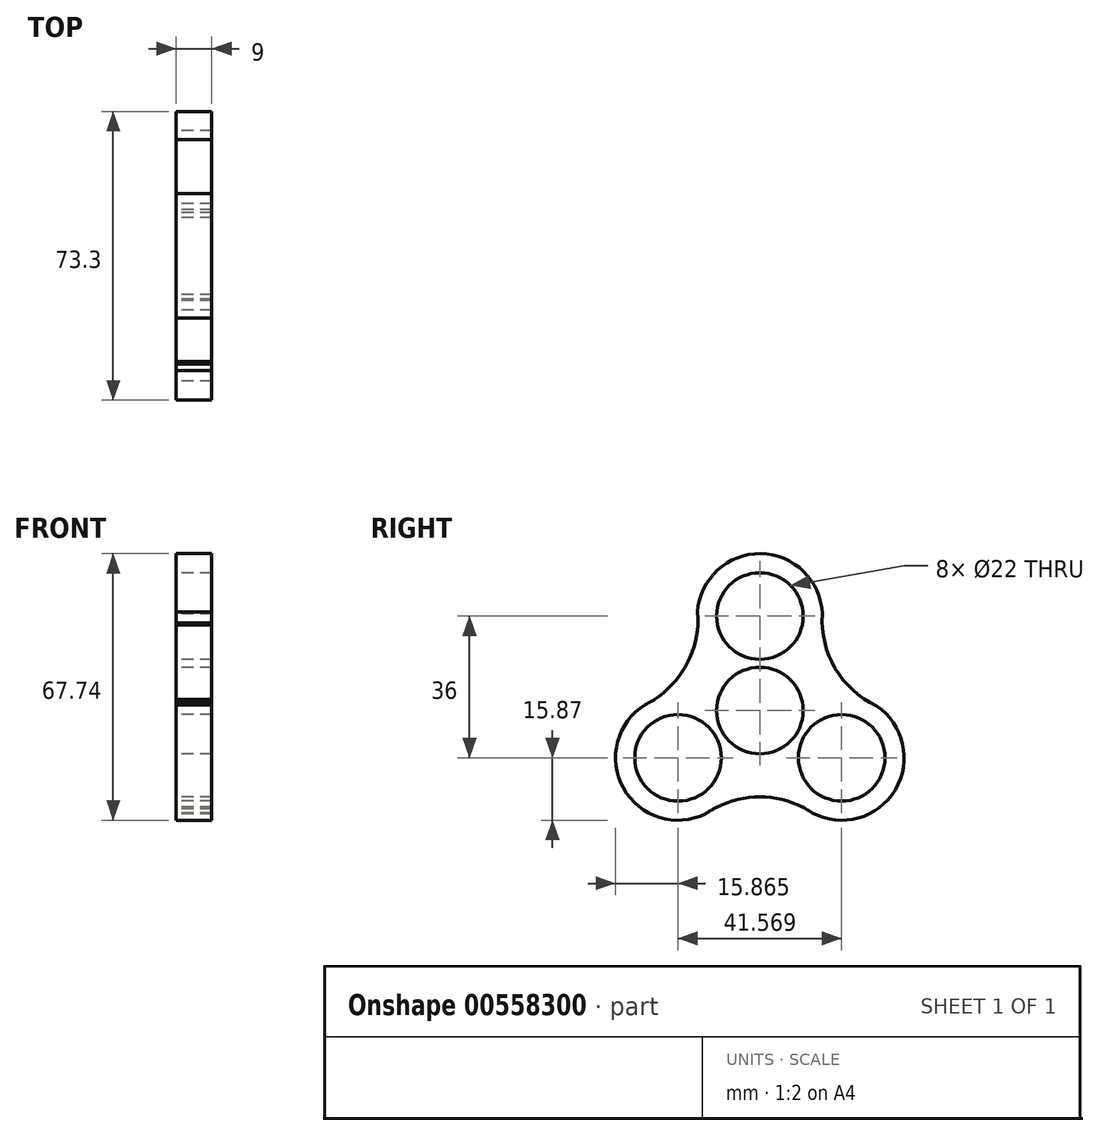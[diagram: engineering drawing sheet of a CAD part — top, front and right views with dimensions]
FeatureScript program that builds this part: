
annotation { "Feature Type Name" : "Feature", "Feature Type Description" : "" }
export const myFeature = defineFeature(function(context is Context, id is Id, definition is map)
    precondition{}
    {
        {
            var Q0;
            Q0=qCreatedBy(makeId("Right.planeOp"),FACE);
            var sketch = newSketch(context, id + "F0", { "sketchPlane" : qUnion([Q0])});
            skLineSegment(sketch, "E0", {"start": v(0, 40) * mm, "end": v(0, 24) * mm});
            skPoint(sketch, "E1", {"position": v(0, 24) * mm});
            skPoint(sketch, "E2.1.0", {"position": v(-20.78, -12) * mm});
            skPoint(sketch, "E2.2.0", {"position": v(20.78, -12) * mm});
            skPoint(sketch, "E2.center", {"position": v(0, 0) * mm});
            skCircle(sketch, "E3", {"center": v(0, 24) * mm, "radius": 11 * mm});
            skCircle(sketch, "E4.1.0", {"center": v(-20.78, -12) * mm, "radius": 11 * mm});
            skCircle(sketch, "E4.2.0", {"center": v(20.78, -12) * mm, "radius": 11 * mm});
            skArc(sketch, "E5.1.0", {"start": v(-26.82, 2.8) * mm, "mid": v(-26.76, 2.76) * mm, "end": v(-26.7, 2.72) * mm});
            skCircle(sketch, "E6", {"center": v(0, 0) * mm, "radius": 11 * mm});
            skPoint(sketch, "E7.start.orphan", {"position": v(10.86, 22.24) * mm});
            skPoint(sketch, "E8.end.orphan", {"position": v(-10.86, 22.24) * mm});
            skArc(sketch, "E9", {"start": v(15.81, 22.66) * mm, "mid": v(-0.46, 39.86) * mm, "end": v(-15.7, 21.76) * mm});
            skArc(sketch, "E10.1.0", {"start": v(-26.7, 2.72) * mm, "mid": v(-34.53, -19.93) * mm, "end": v(-10.99, -24.48) * mm});
            skArc(sketch, "E10.2.0", {"start": v(10.99, -24.48) * mm, "mid": v(34.41, -20.13) * mm, "end": v(27.11, 2.55) * mm});
            skPoint(sketch, "E11.orphan", {"position": v(-11.53, -17.94) * mm});
            skArc(sketch, "E12", {"start": v(15.86, 24.5) * mm, "mid": v(19.14, 10.73) * mm, "end": v(29.6, 1.2) * mm});
            skPoint(sketch, "E12.first.point", {"position": v(15.86, 24.5) * mm});
            skPoint(sketch, "E12.second.point", {"position": v(29.6, 1.2) * mm});
            skPoint(sketch, "E12.third.point", {"position": v(63.5, 27.41) * mm});
            skArc(sketch, "E13.1.0", {"start": v(-29.15, 1.49) * mm, "mid": v(-18.86, 11.21) * mm, "end": v(-15.83, 25.04) * mm});
            skArc(sketch, "E13.2.0", {"start": v(13.29, -25.98) * mm, "mid": v(-0.28, -21.94) * mm, "end": v(-13.77, -26.23) * mm});
            skPoint(sketch, "E14.orphan", {"position": v(-10.08, 9.49) * mm});
            skArc(sketch, "E15.trimOffspring", {"start": v(-15.7, 21.76) * mm, "mid": v(-15.75, 21.78) * mm, "end": v(-15.78, 21.8) * mm});
            skArc(sketch, "E16.trimOffspring", {"start": v(10.98, -24.63) * mm, "mid": v(10.99, -24.55) * mm, "end": v(10.99, -24.48) * mm});
            skArc(sketch, "E17.trimOffspring", {"start": v(-10.99, -24.48) * mm, "mid": v(-10.99, -24.53) * mm, "end": v(-10.99, -24.57) * mm});
            skSolve(sketch);
        }
        {
            var Q0;
            Q0=makeQuery(id+"F0.imprint","IMPRINT",FACE,{"disambiguationData":[TD([[makeQuery(id+"F0.imprint","IMPRINT",EDGE,{"derivedFrom":sQuery(id+"F0.wireOp",EDGE,"E3")}),-1.0]])]});
            var Q1;
            Q1=sQuery(id+"F0.wireOp",EDGE,"E13.1.0");
            var Q2;
            Q2=sQuery(id+"F0.wireOp",EDGE,"E9");
            var Q3;
            Q3=sQuery(id+"F0.wireOp",EDGE,"E12");
            var Q4;
            Q4=sQuery(id+"F0.wireOp",EDGE,"E10.2.0");
            var Q5;
            Q5=sQuery(id+"F0.wireOp",EDGE,"E13.2.0");
            var Q6;
            Q6=sQuery(id+"F0.wireOp",EDGE,"E10.1.0");
            var Q7;
            Q7=sQuery(id+"F0.wireOp",EDGE,"E6");
            var Q8;
            Q8=sQuery(id+"F0.wireOp",EDGE,"E3");
            var Q9;
            Q9=sQuery(id+"F0.wireOp",EDGE,"E4.2.0");
            var Q10;
            Q10=sQuery(id+"F0.wireOp",EDGE,"E4.1.0");
            extrude(context, id + "F1", {"entities" : qUnion([Q0]), "surfaceEntities" : qUnion([Q1, Q2, Q3, Q4, Q5, Q6, Q7, Q8, Q9, Q10]), "depth" : 9 * mm, "offsetDistance" : 25 * mm});
        }
    });
